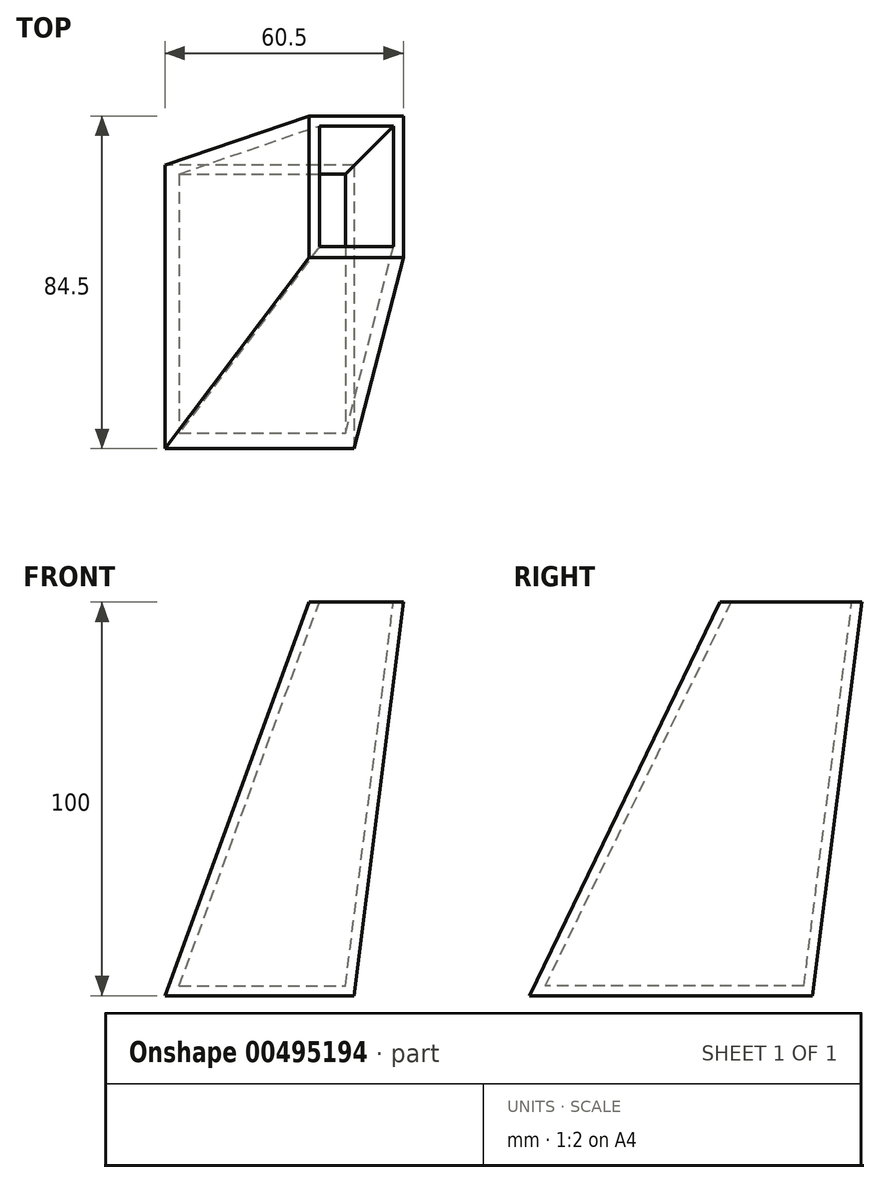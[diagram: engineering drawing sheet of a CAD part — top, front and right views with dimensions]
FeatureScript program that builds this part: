
annotation { "Feature Type Name" : "Feature", "Feature Type Description" : "" }
export const myFeature = defineFeature(function(context is Context, id is Id, definition is map)
    precondition{}
    {
        {
            var Q0;
            Q0=qCreatedBy(makeId("Top.planeOp"),FACE);
            var sketch = newSketch(context, id + "F0", { "sketchPlane" : qUnion([Q0])});
            skLineSegment(sketch, "E0.bottom", {"start": v(12.5, 48.5) * mm, "end": v(36.5, 48.5) * mm});
            skLineSegment(sketch, "E0.top", {"start": v(12.5, 12.5) * mm, "end": v(36.5, 12.5) * mm});
            skLineSegment(sketch, "E0.left", {"start": v(12.5, 48.5) * mm, "end": v(12.5, 12.5) * mm});
            skLineSegment(sketch, "E0.right", {"start": v(36.5, 48.5) * mm, "end": v(36.5, 12.5) * mm});
            skPoint(sketch, "E0.middle", {"position": v(0, 0) * mm});
            skSolve(sketch);
        }
        {
            assignVariable(context, id + "F1", {"variableType" : VariableType.LENGTH, "name" : "z", "lengthValue" : 100 * mm});
        }
        {
            var Q0;
            Q0=qCreatedBy(makeId("Top.planeOp"),FACE);
            cPlane(context, id + "F2", {"entities" : qUnion([Q0]), "cplaneType" : CPlaneType.OFFSET, "offset" : getVariable(context, 'z'), "oppositeDirection" : true, "width" : 150 * mm, "height" : 150 * mm});
        }
        {
            var Q0;
            Q0=qCreatedBy(id+"F2.planeOp",FACE);
            var sketch = newSketch(context, id + "F3", { "sketchPlane" : qUnion([Q0])});
            skPoint(sketch, "E1.0", {"position": v(0, 0) * mm});
            skLineSegment(sketch, "E2.bottom", {"start": v(24, 36) * mm, "end": v(-24, 36) * mm});
            skLineSegment(sketch, "E2.top", {"start": v(24, -36) * mm, "end": v(-24, -36) * mm});
            skLineSegment(sketch, "E2.left", {"start": v(24, 36) * mm, "end": v(24, -36) * mm});
            skLineSegment(sketch, "E2.right", {"start": v(-24, 36) * mm, "end": v(-24, -36) * mm});
            skSolve(sketch);
        }
        {
            var Q0;
            Q0=makeQuery(id+"F0.imprint","IMPRINT",FACE,{"disambiguationData":[TD([[makeQuery(id+"F0.imprint","IMPRINT",EDGE,{"derivedFrom":sQuery(id+"F0.wireOp",EDGE,"E0.bottom")}),-1.0]])]});
            var Q1;
            Q1=makeQuery(id+"F3.imprint","IMPRINT",FACE,{"disambiguationData":[TD([[makeQuery(id+"F3.imprint","IMPRINT",EDGE,{"derivedFrom":sQuery(id+"F3.wireOp",EDGE,"E2.bottom")}),1.0]])]});
            loft(context, id + "F4", {"sheetProfilesArray" : [{ "sheetProfileEntities" : qUnion([Q0]) }, { "sheetProfileEntities" : qUnion([Q1]) }]});
        }
        {
            var Q0;
            Q0=makeQuery(id+"F4.opLoft","CAP_FACE",FACE,{"disambiguationData":[OSD([makeQuery(id+"F0.imprint","IMPRINT",FACE,{"disambiguationData":[TD([[makeQuery(id+"F0.imprint","IMPRINT",EDGE,{"derivedFrom":sQuery(id+"F0.wireOp",EDGE,"E0.bottom")}),-1.0]])]})])],"isStart":true});
            var Q1;
            Q1=makeQuery(id+"F4.opLoft","CAP_FACE",FACE,{"disambiguationData":[OSD([makeQuery(id+"F3.imprint","IMPRINT",FACE,{"disambiguationData":[TD([[makeQuery(id+"F3.imprint","IMPRINT",EDGE,{"derivedFrom":sQuery(id+"F3.wireOp",EDGE,"E2.bottom")}),1.0]])]})])],"isStart":true});
            shell(context, id + "F5", {"entities" : qUnion([Q0, Q1]), "thickness" : 2.5 * mm});
        }
    });
